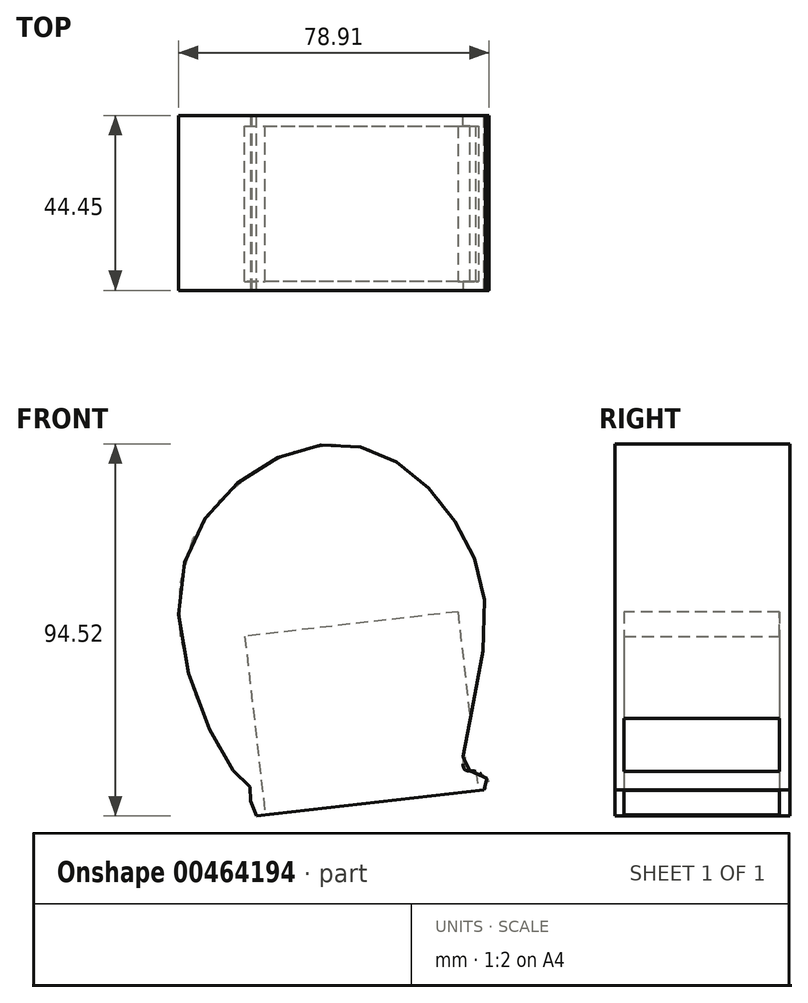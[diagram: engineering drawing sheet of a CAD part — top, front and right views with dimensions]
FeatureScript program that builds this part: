
annotation { "Feature Type Name" : "Feature", "Feature Type Description" : "" }
export const myFeature = defineFeature(function(context is Context, id is Id, definition is map)
    precondition{}
    {
        {
            var Q0;
            Q0=qCreatedBy(makeId("Front.planeOp"),FACE);
            var sketch = newSketch(context, id + "F0", { "sketchPlane" : qUnion([Q0])});
            skFitSpline(sketch, "E0", {"points": [v(-52.7, -38.03) * mm, v(-54.29, -34.56) * mm, v(-53.97, -31.4) * mm, v(-57.44, -27.93) * mm, v(-72.24, 9) * mm, v(-62.5, 41.82) * mm, v(-36.61, 56.2) * mm, v(-16.1, 51.29) * mm, v(0, 32.98) * mm, v(5.05, 5.84) * mm, v(0, -26.04) * mm, v(2.84, -26.67) * mm, v(6.31, -29.51) * mm, v(5.05, -31.4) * mm], "startDerivative": vector(-58.11, 85.23) * mm, "endDerivative": vector(-67.73, -55.7) * mm});
            skLineSegment(sketch, "E1", {"start": v(-52.7, -38.03) * mm, "end": v(5.05, -31.4) * mm});
            skSolve(sketch);
        }
        {
            var Q0;
            Q0=makeQuery(id+"F0.imprint","IMPRINT",FACE,{"disambiguationData":[TD([[makeQuery(id+"F0.imprint","IMPRINT",EDGE,{"derivedFrom":sQuery(id+"F0.wireOp",EDGE,"E0")}),-1.0]])]});
            extrude(context, id + "F1", {"entities" : qUnion([Q0]), "depth" : 44.45 * mm});
        }
        {
            var Q0;
            Q0=makeQuery(id+"F1.opExtrude","SWEPT_FACE",FACE,{"disambiguationData":[OSD([sQuery(id+"F0.wireOp",EDGE,"E1")])]});
            var sketch = newSketch(context, id + "F2", { "sketchPlane" : qUnion([Q0])});
            skLineSegment(sketch, "E2", {"start": v(-54.48, 42.14) * mm, "end": v(-54.48, 2.68) * mm});
            skLineSegment(sketch, "E3", {"start": v(-54.48, 2.68) * mm, "end": v(0, 2.68) * mm});
            skLineSegment(sketch, "E4", {"start": v(0, 2.68) * mm, "end": v(0, 42.14) * mm});
            skLineSegment(sketch, "E5", {"start": v(0, 42.14) * mm, "end": v(-54.48, 42.14) * mm});
            skSolve(sketch);
        }
        {
            var Q0;
            Q0 = qSketchRegion(id + "F2", true);
            extrude(context, id + "F3", {"entities" : qUnion([Q0]), "operationType" : NewBodyOperationType.REMOVE, "oppositeDirection" : true, "depth" : 45.72 * mm});
        }
    });
